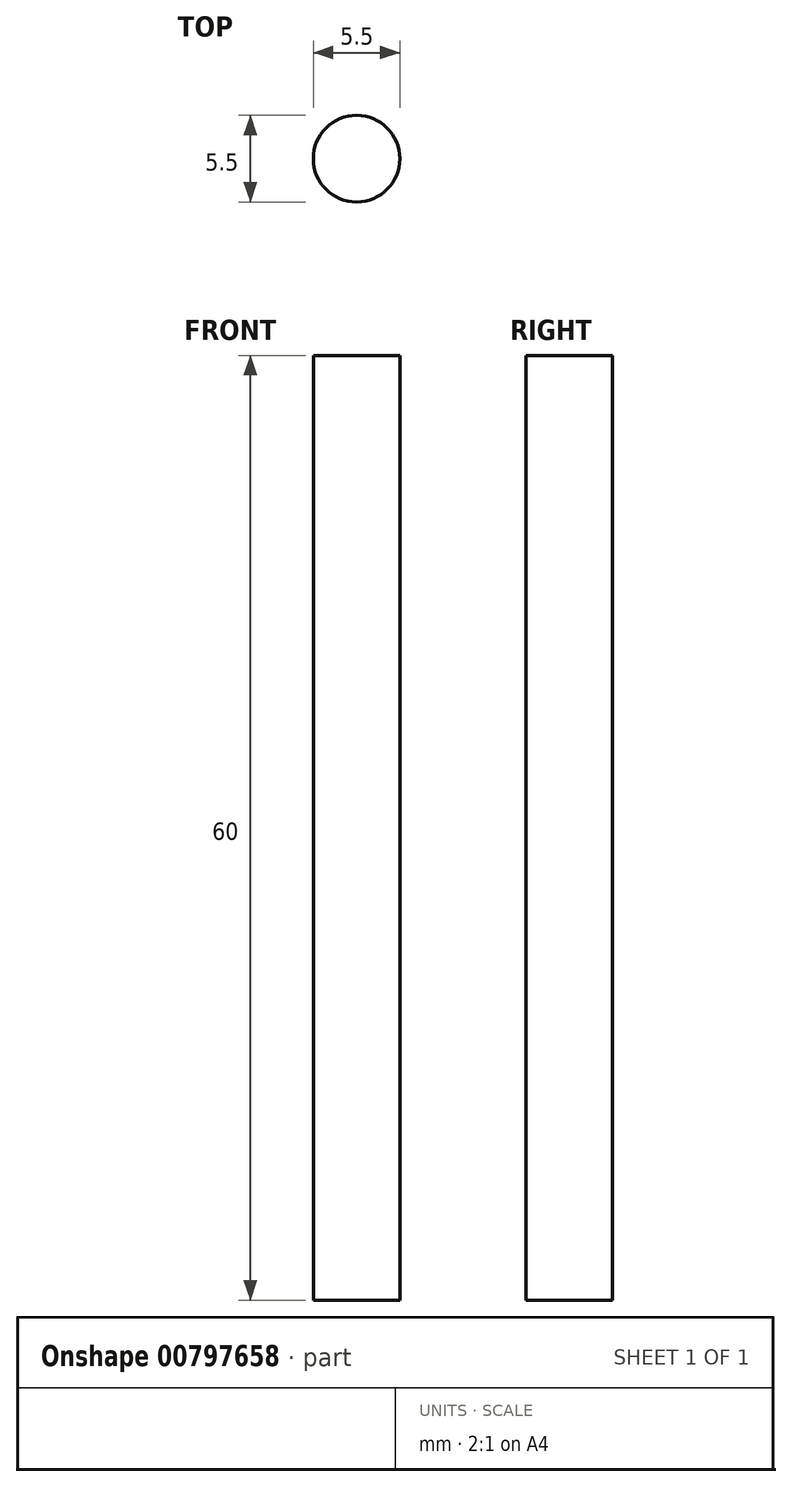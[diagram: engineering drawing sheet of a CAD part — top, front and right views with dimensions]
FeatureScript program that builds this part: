
annotation { "Feature Type Name" : "Feature", "Feature Type Description" : "" }
export const myFeature = defineFeature(function(context is Context, id is Id, definition is map)
    precondition{}
    {
        {
            var Q0;
            Q0=qCreatedBy(makeId("Top.planeOp"),FACE);
            var sketch = newSketch(context, id + "F0", { "sketchPlane" : qUnion([Q0])});
            skCircle(sketch, "E0", {"center": v(0, 0) * mm, "radius": 2.75 * mm});
            skSolve(sketch);
        }
        {
            var Q0;
            Q0=qSketchRegion(id+"F0",true);
            extrude(context, id + "F1", {"entities" : qUnion([Q0]), "depth" : 60 * mm, "offsetDistance" : 25 * mm});
        }
    });
